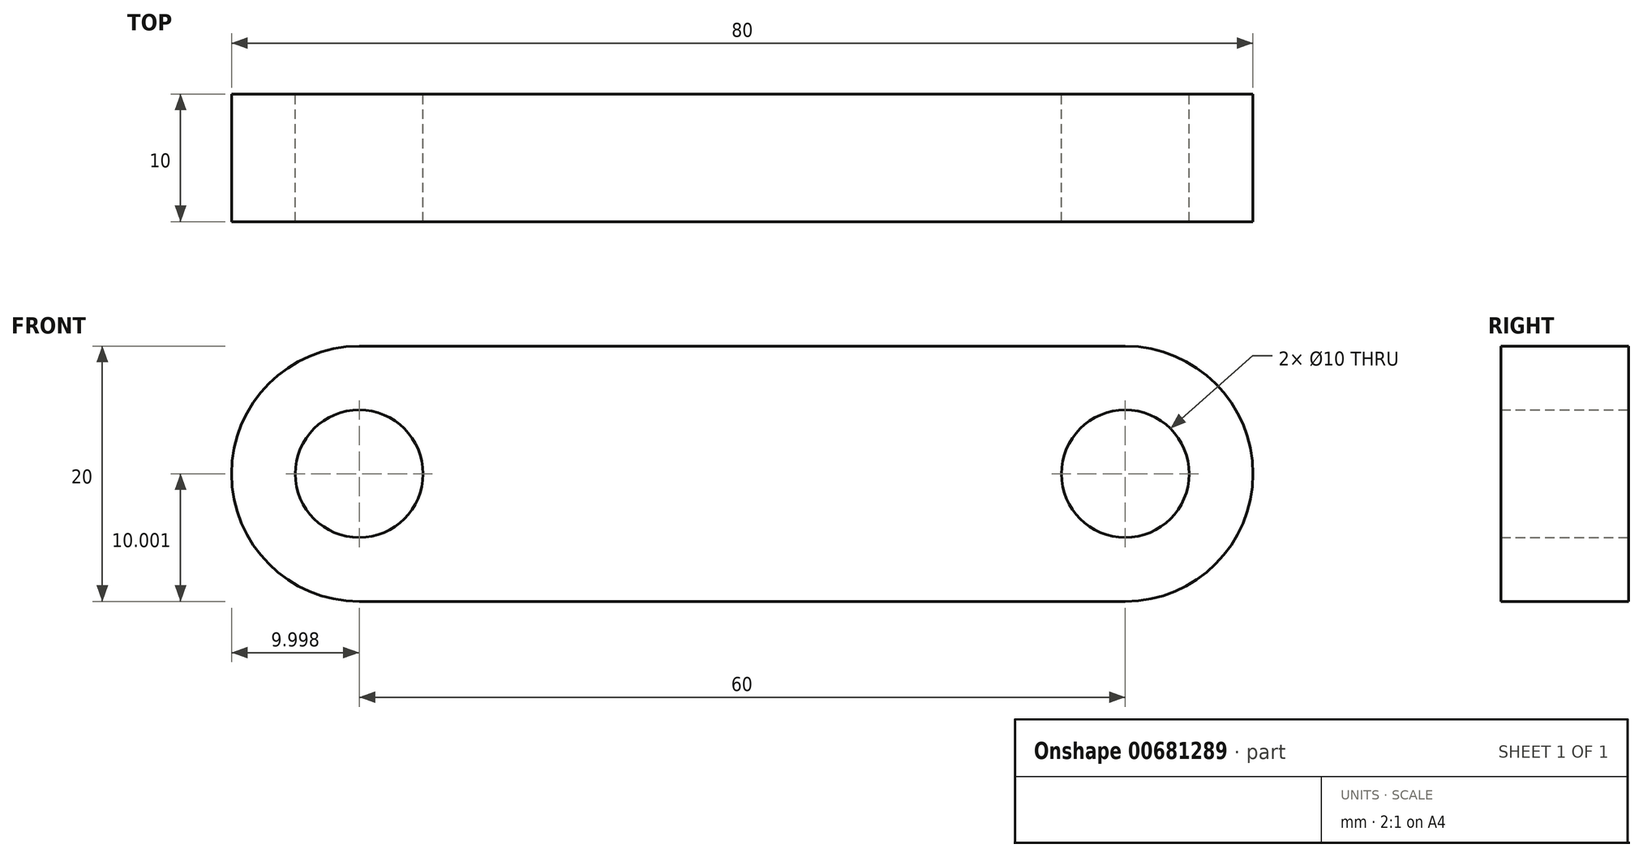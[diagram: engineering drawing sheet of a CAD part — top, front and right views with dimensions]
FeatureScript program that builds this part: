
annotation { "Feature Type Name" : "Feature", "Feature Type Description" : "" }
export const myFeature = defineFeature(function(context is Context, id is Id, definition is map)
    precondition{}
    {
        {
            var Q0;
            Q0=qCreatedBy(makeId("Front.planeOp"),FACE);
            var sketch = newSketch(context, id + "F0", { "sketchPlane" : qUnion([Q0])});
            skLineSegment(sketch, "E0.bottom", {"start": v(-20.8, 9.17) * mm, "end": v(39.2, 9.17) * mm});
            skLineSegment(sketch, "E0.top", {"start": v(-20.8, -10.83) * mm, "end": v(39.2, -10.83) * mm});
            skArc(sketch, "E1", {"start": v(-20.8, 9.17) * mm, "mid": v(-30.8, -0.83) * mm, "end": v(-20.8, -10.83) * mm});
            skArc(sketch, "E2", {"start": v(39.2, -10.83) * mm, "mid": v(49.2, -0.83) * mm, "end": v(39.2, 9.17) * mm});
            skCircle(sketch, "E3", {"center": v(-20.8, -0.83) * mm, "radius": 5 * mm});
            skCircle(sketch, "E4", {"center": v(39.2, -0.83) * mm, "radius": 5 * mm});
            skSolve(sketch);
        }
        {
            var Q0;
            Q0=makeQuery(id+"F0.imprint","IMPRINT",FACE,{"disambiguationData":[TD([[makeQuery(id+"F0.imprint","IMPRINT",EDGE,{"derivedFrom":sQuery(id+"F0.wireOp",EDGE,"E0.bottom")}),-1.0]])]});
            extrude(context, id + "F1", {"entities" : qUnion([Q0]), "depth" : 10 * mm, "offsetDistance" : 25 * mm});
        }
    });
